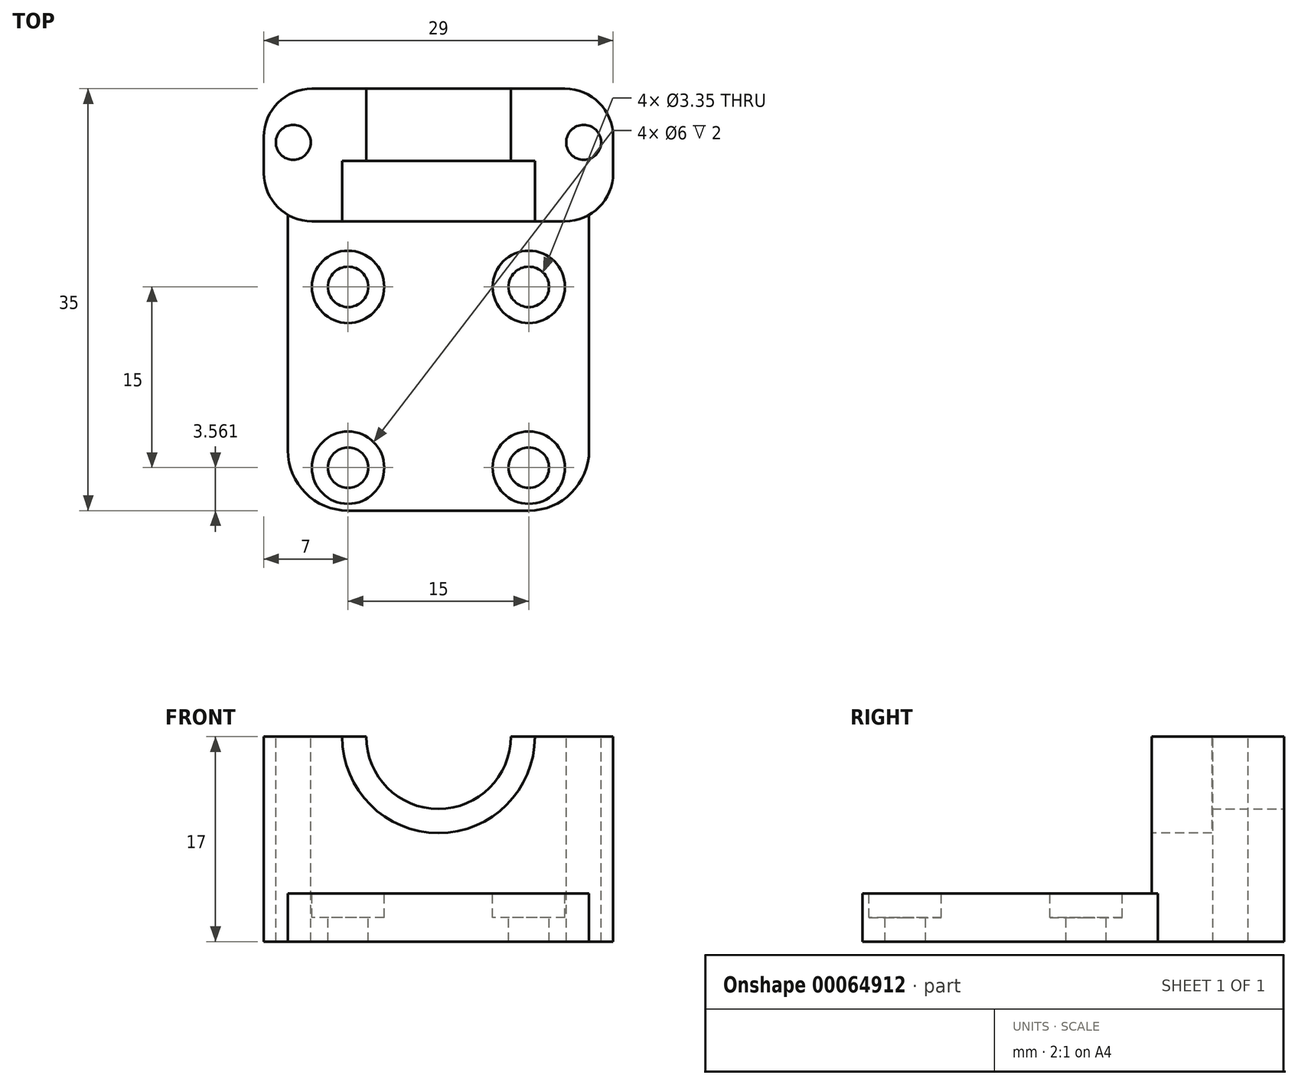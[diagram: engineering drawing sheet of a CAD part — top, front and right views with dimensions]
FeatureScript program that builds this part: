
annotation { "Feature Type Name" : "Feature", "Feature Type Description" : "" }
export const myFeature = defineFeature(function(context is Context, id is Id, definition is map)
    precondition{}
    {
        {
            var Q0;
            Q0=qCreatedBy(makeId("Top.planeOp"),FACE);
            var sketch = newSketch(context, id + "F0", { "sketchPlane" : qUnion([Q0])});
            skLineSegment(sketch, "E0.bottom", {"start": v(0, 0) * mm, "end": v(25, 0) * mm});
            skLineSegment(sketch, "E0.top", {"start": v(0, 35) * mm, "end": v(25, 35) * mm});
            skLineSegment(sketch, "E0.left", {"start": v(0, 0) * mm, "end": v(0, 35) * mm});
            skLineSegment(sketch, "E0.right", {"start": v(25, 0) * mm, "end": v(25, 35) * mm});
            skSolve(sketch);
        }
        {
            var Q0;
            Q0=qSketchRegion(id+"F0",true);
            extrude(context, id + "F1", {"entities" : qUnion([Q0]), "depth" : 4 * mm});
        }
        {
            var Q0;
            Q0=makeQuery(id+"F1.opExtrude","CAP_FACE",FACE,{"disambiguationData":[OSD([sQuery(id+"F0.wireOp",EDGE,"E0.bottom"),sQuery(id+"F0.wireOp",EDGE,"E0.top"),sQuery(id+"F0.wireOp",EDGE,"E0.left"),sQuery(id+"F0.wireOp",EDGE,"E0.right")])],"isStart":false});
            var sketch = newSketch(context, id + "F2", { "sketchPlane" : qUnion([Q0])});
            skCircle(sketch, "E1", {"center": v(5, 18.56) * mm, "radius": 1.68 * mm});
            skCircle(sketch, "E2", {"center": v(20, 18.56) * mm, "radius": 1.68 * mm});
            skCircle(sketch, "E3", {"center": v(5, 3.56) * mm, "radius": 1.68 * mm});
            skCircle(sketch, "E4", {"center": v(20, 3.56) * mm, "radius": 1.68 * mm});
            skLineSegment(sketch, "E5", {"start": v(5, 18.56) * mm, "end": v(0, 18.56) * mm});
            skLineSegment(sketch, "E6", {"start": v(20, 3.56) * mm, "end": v(25, 3.56) * mm});
            skCircle(sketch, "E7", {"center": v(5, 18.56) * mm, "radius": 3 * mm});
            skCircle(sketch, "E8", {"center": v(20, 18.56) * mm, "radius": 3 * mm});
            skCircle(sketch, "E9", {"center": v(5, 3.56) * mm, "radius": 3 * mm});
            skCircle(sketch, "E10", {"center": v(20, 3.56) * mm, "radius": 3 * mm});
            skSolve(sketch);
        }
        {
            var Q0;
            Q0=makeQuery(id+"F2.imprint","IMPRINT",FACE,{"disambiguationData":[TD([[makeQuery(id+"F2.imprint","IMPRINT",EDGE,{"derivedFrom":sQuery(id+"F2.wireOp",EDGE,"E1")}),1.0]])]});
            var Q1;
            Q1=makeQuery(id+"F2.imprint","IMPRINT",FACE,{"disambiguationData":[TD([[makeQuery(id+"F2.imprint","IMPRINT",EDGE,{"derivedFrom":sQuery(id+"F2.wireOp",EDGE,"E2")}),1.0]])]});
            var Q2;
            Q2=makeQuery(id+"F2.imprint","IMPRINT",FACE,{"disambiguationData":[TD([[makeQuery(id+"F2.imprint","IMPRINT",EDGE,{"derivedFrom":sQuery(id+"F2.wireOp",EDGE,"E4")}),1.0]])]});
            var Q3;
            Q3=makeQuery(id+"F2.imprint","IMPRINT",FACE,{"disambiguationData":[TD([[makeQuery(id+"F2.imprint","IMPRINT",EDGE,{"derivedFrom":sQuery(id+"F2.wireOp",EDGE,"E3")}),1.0]])]});
            extrude(context, id + "F3", {"entities" : qUnion([Q0, Q1, Q2, Q3]), "operationType" : NewBodyOperationType.REMOVE, "oppositeDirection" : true, "depth" : 25 * mm});
        }
        {
            var Q0;
            Q0=makeQuery(id+"F1.opExtrude","CAP_FACE",FACE,{"disambiguationData":[OSD([sQuery(id+"F0.wireOp",EDGE,"E0.bottom"),sQuery(id+"F0.wireOp",EDGE,"E0.top"),sQuery(id+"F0.wireOp",EDGE,"E0.left"),sQuery(id+"F0.wireOp",EDGE,"E0.right")])],"isStart":false});
            var sketch = newSketch(context, id + "F4", { "sketchPlane" : qUnion([Q0])});
            skLineSegment(sketch, "E11.bottom", {"start": v(0, 35) * mm, "end": v(25, 35) * mm});
            skLineSegment(sketch, "E11.top", {"start": v(0, 24) * mm, "end": v(25, 24) * mm});
            skLineSegment(sketch, "E11.left", {"start": v(0, 35) * mm, "end": v(0, 24) * mm});
            skLineSegment(sketch, "E11.right", {"start": v(25, 35) * mm, "end": v(25, 24) * mm});
            skSolve(sketch);
        }
        {
            var Q0;
            Q0=qSketchRegion(id+"F4",true);
            extrude(context, id + "F5", {"entities" : qUnion([Q0]), "operationType" : NewBodyOperationType.ADD, "depth" : 13 * mm});
        }
        {
            var Q0;
            Q0=makeQuery(id+"F5.boolean.opBoolean","MERGE",FACE,{"derivedFrom":[makeQuery(id+"F1.opExtrude","SWEPT_FACE",FACE,{"disambiguationData":[OSD([sQuery(id+"F0.wireOp",EDGE,"E0.top")])]}),makeQuery(id+"F5.opExtrude","SWEPT_FACE",FACE,{"disambiguationData":[OSD([sQuery(id+"F4.wireOp",EDGE,"E11.bottom")])]})]});
            var sketch = newSketch(context, id + "F6", { "sketchPlane" : qUnion([Q0])});
            skCircle(sketch, "E12", {"center": v(-12.5, 17) * mm, "radius": 6 * mm});
            skSolve(sketch);
        }
        {
            var Q0;
            {var subQ0=makeQuery(id+"F5.opExtrude","CAP_EDGE",EDGE,{"disambiguationData":[OSD([sQuery(id+"F4.wireOp",EDGE,"E11.bottom")])],"isStart":false});var subQ1=sQuery(id+"F6.wireOp",EDGE,"E12");var subQ3=makeQuery(id+"F6.imprint","INTERSECT",VERTEX,{"disambiguationData":[OD(0.0)],"derivedFrom":[subQ0,subQ1]});Q0=makeQuery(id+"F6.imprint","IMPRINT",FACE,{"disambiguationData":[TD([[makeQuery(id+"F6.imprint","IMPRINT",EDGE,{"disambiguationData":[TD([[subQ3,1.0]])],"derivedFrom":subQ1}),1.0]])]});}
            extrude(context, id + "F7", {"entities" : qUnion([Q0]), "operationType" : NewBodyOperationType.REMOVE, "oppositeDirection" : true, "depth" : 6 * mm});
        }
        {
            var Q0;
            Q0=makeQuery(id+"F5.opExtrude","SWEPT_FACE",FACE,{"disambiguationData":[OSD([sQuery(id+"F4.wireOp",EDGE,"E11.top")])]});
            var sketch = newSketch(context, id + "F8", { "sketchPlane" : qUnion([Q0])});
            skCircle(sketch, "E13", {"center": v(12.5, 17) * mm, "radius": 8 * mm});
            skSolve(sketch);
        }
        {
            var Q0;
            Q0=qSketchRegion(id+"F8",true);
            extrude(context, id + "F9", {"entities" : qUnion([Q0]), "operationType" : NewBodyOperationType.REMOVE, "oppositeDirection" : true, "depth" : 5 * mm});
        }
        {
            var Q0;
            Q0=makeQuery(id+"F2.imprint","IMPRINT",FACE,{"disambiguationData":[TD([[makeQuery(id+"F2.imprint","IMPRINT",EDGE,{"derivedFrom":sQuery(id+"F2.wireOp",EDGE,"E1")}),-1.0]])]});
            var Q1;
            Q1=makeQuery(id+"F2.imprint","IMPRINT",FACE,{"disambiguationData":[TD([[makeQuery(id+"F2.imprint","IMPRINT",EDGE,{"derivedFrom":sQuery(id+"F2.wireOp",EDGE,"E2")}),-1.0]])]});
            var Q2;
            Q2=makeQuery(id+"F2.imprint","IMPRINT",FACE,{"disambiguationData":[TD([[makeQuery(id+"F2.imprint","IMPRINT",EDGE,{"derivedFrom":sQuery(id+"F2.wireOp",EDGE,"E4")}),-1.0]])]});
            var Q3;
            Q3=makeQuery(id+"F2.imprint","IMPRINT",FACE,{"disambiguationData":[TD([[makeQuery(id+"F2.imprint","IMPRINT",EDGE,{"derivedFrom":sQuery(id+"F2.wireOp",EDGE,"E3")}),-1.0]])]});
            extrude(context, id + "F10", {"entities" : qUnion([Q0, Q1, Q2, Q3]), "operationType" : NewBodyOperationType.REMOVE, "oppositeDirection" : true, "depth" : 2 * mm});
        }
        {
            var Q0;
            Q0=makeQuery(id+"F1.opExtrude","SWEPT_EDGE",EDGE,{"disambiguationData":[OSD([sQuery(id+"F0.wireOp",EDGE,"E0.bottom"),sQuery(id+"F0.wireOp",EDGE,"E0.left")])]});
            var Q1;
            Q1=makeQuery(id+"F1.opExtrude","SWEPT_EDGE",EDGE,{"disambiguationData":[OSD([sQuery(id+"F0.wireOp",EDGE,"E0.bottom"),sQuery(id+"F0.wireOp",EDGE,"E0.right")])]});
            fillet(context, id + "F11", {"entities" : qUnion([Q0, Q1]), "radius" : 5 * mm, "tangentPropagation" : true, "allowEdgeOverflow" : false});
        }
        {
            var Q0;
            Q0=makeQuery(id+"F5.boolean.opBoolean","MERGE",FACE,{"derivedFrom":[makeQuery(id+"F1.opExtrude","SWEPT_FACE",FACE,{"disambiguationData":[OSD([sQuery(id+"F0.wireOp",EDGE,"E0.left")])]}),makeQuery(id+"F5.opExtrude","SWEPT_FACE",FACE,{"disambiguationData":[OSD([sQuery(id+"F4.wireOp",EDGE,"E11.left")])]})]});
            var sketch = newSketch(context, id + "F12", { "sketchPlane" : qUnion([Q0])});
            skLineSegment(sketch, "E14.bottom", {"start": v(-35, 0) * mm, "end": v(-24, 0) * mm});
            skLineSegment(sketch, "E14.top", {"start": v(-35, 17) * mm, "end": v(-24, 17) * mm});
            skLineSegment(sketch, "E14.left", {"start": v(-35, 0) * mm, "end": v(-35, 17) * mm});
            skLineSegment(sketch, "E14.right", {"start": v(-24, 0) * mm, "end": v(-24, 17) * mm});
            skSolve(sketch);
        }
        {
            var Q0;
            Q0=qSketchRegion(id+"F12",true);
            extrude(context, id + "F13", {"entities" : qUnion([Q0]), "operationType" : NewBodyOperationType.ADD, "depth" : 2 * mm});
        }
        {
            var Q0;
            Q0=makeQuery(id+"F5.boolean.opBoolean","MERGE",FACE,{"derivedFrom":[makeQuery(id+"F1.opExtrude","SWEPT_FACE",FACE,{"disambiguationData":[OSD([sQuery(id+"F0.wireOp",EDGE,"E0.right")])]}),makeQuery(id+"F5.opExtrude","SWEPT_FACE",FACE,{"disambiguationData":[OSD([sQuery(id+"F4.wireOp",EDGE,"E11.right")])]})]});
            var sketch = newSketch(context, id + "F14", { "sketchPlane" : qUnion([Q0])});
            skLineSegment(sketch, "E15.bottom", {"start": v(35, 0) * mm, "end": v(24, 0) * mm});
            skLineSegment(sketch, "E15.top", {"start": v(35, 17) * mm, "end": v(24, 17) * mm});
            skLineSegment(sketch, "E15.left", {"start": v(35, 0) * mm, "end": v(35, 17) * mm});
            skLineSegment(sketch, "E15.right", {"start": v(24, 0) * mm, "end": v(24, 17) * mm});
            skSolve(sketch);
        }
        {
            var Q0;
            Q0=qSketchRegion(id+"F14",true);
            extrude(context, id + "F15", {"entities" : qUnion([Q0]), "operationType" : NewBodyOperationType.ADD, "depth" : 2 * mm});
        }
        {
            var Q0;
            {var subQ0=sQuery(id+"F4.wireOp",EDGE,"E11.bottom");var subQ1=sQuery(id+"F4.wireOp",EDGE,"E11.top");var subQ2=sQuery(id+"F4.wireOp",EDGE,"E11.left");Q0=makeQuery(id+"F9.boolean.opBoolean","SPLIT",FACE,{"disambiguationData":[TD([makeQuery(id+"F1.opExtrude","SWEPT_FACE",FACE,{"disambiguationData":[OSD([sQuery(id+"F0.wireOp",EDGE,"E0.left")])]})])],"derivedFrom":makeQuery(id+"F5.opExtrude","CAP_FACE",FACE,{"disambiguationData":[OSD([subQ0,subQ1,subQ2,sQuery(id+"F4.wireOp",EDGE,"E11.right")])],"isStart":false})});}
            var sketch = newSketch(context, id + "F16", { "sketchPlane" : qUnion([Q0])});
            skCircle(sketch, "E16", {"center": v(0.45, 30.55) * mm, "radius": 1.45 * mm});
            skCircle(sketch, "E17", {"center": v(24.55, 30.55) * mm, "radius": 1.45 * mm});
            skSolve(sketch);
        }
        {
            var Q0;
            Q0=qSketchRegion(id+"F16",true);
            extrude(context, id + "F17", {"entities" : qUnion([Q0]), "operationType" : NewBodyOperationType.REMOVE, "oppositeDirection" : true, "depth" : 25 * mm});
        }
        {
            var Q0;
            Q0=makeQuery(id+"F13.opExtrude","CAP_EDGE",EDGE,{"disambiguationData":[OSD([sQuery(id+"F12.wireOp",EDGE,"E14.right")])],"isStart":false});
            var Q1;
            Q1=makeQuery(id+"F13.opExtrude","CAP_EDGE",EDGE,{"disambiguationData":[OSD([sQuery(id+"F12.wireOp",EDGE,"E14.left")])],"isStart":false});
            var Q2;
            Q2=makeQuery(id+"F15.opExtrude","CAP_EDGE",EDGE,{"disambiguationData":[OSD([sQuery(id+"F14.wireOp",EDGE,"E15.left")])],"isStart":false});
            var Q3;
            Q3=makeQuery(id+"F15.opExtrude","CAP_EDGE",EDGE,{"disambiguationData":[OSD([sQuery(id+"F14.wireOp",EDGE,"E15.right")])],"isStart":false});
            fillet(context, id + "F18", {"entities" : qUnion([Q0, Q1, Q2, Q3]), "radius" : 4 * mm, "allowEdgeOverflow" : false});
        }
    });
